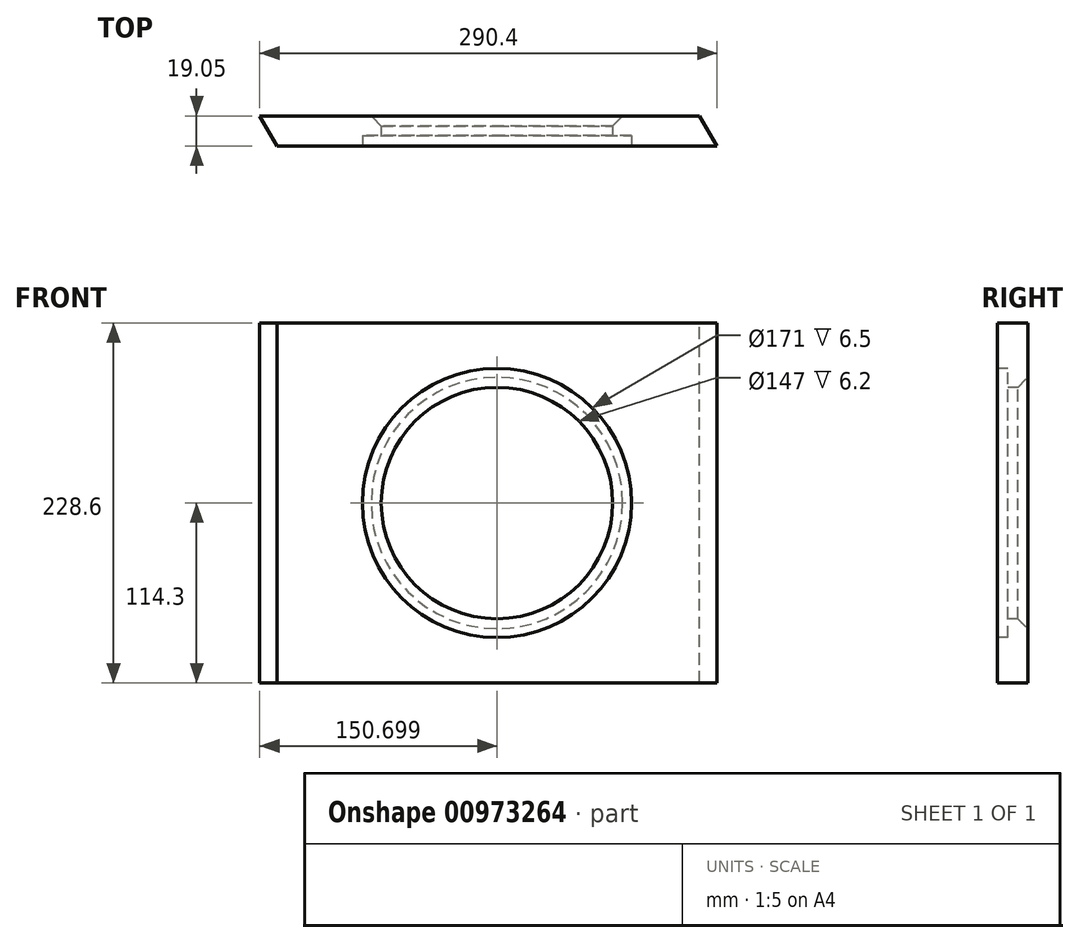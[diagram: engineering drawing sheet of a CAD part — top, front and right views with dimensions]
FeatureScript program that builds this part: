
annotation { "Feature Type Name" : "Feature", "Feature Type Description" : "" }
export const myFeature = defineFeature(function(context is Context, id is Id, definition is map)
    precondition{}
    {
        {
            var Q0;
            Q0=qCreatedBy(makeId("Front.planeOp"),FACE);
            var sketch = newSketch(context, id + "F0", { "sketchPlane" : qUnion([Q0])});
            skLineSegment(sketch, "E0.bottom", {"start": v(145.2, -114.3) * mm, "end": v(-145.2, -114.3) * mm});
            skLineSegment(sketch, "E0.top", {"start": v(145.2, 114.3) * mm, "end": v(-145.2, 114.3) * mm});
            skLineSegment(sketch, "E0.left", {"start": v(145.2, -114.3) * mm, "end": v(145.2, 114.3) * mm});
            skLineSegment(sketch, "E0.right", {"start": v(-145.2, -114.3) * mm, "end": v(-145.2, 114.3) * mm});
            skPoint(sketch, "E0.middle", {"position": v(0, 0) * mm});
            skSolve(sketch);
        }
        {
            var Q0;
            Q0=makeQuery(id+"F0.imprint","IMPRINT",FACE,{"disambiguationData":[TD([[makeQuery(id+"F0.imprint","IMPRINT",EDGE,{"derivedFrom":sQuery(id+"F0.wireOp",EDGE,"E0.bottom")}),-1.0]])]});
            extrude(context, id + "F1", {"entities" : qUnion([Q0]), "depth" : 19.05 * mm, "offsetDistance" : 25.4 * mm});
        }
        {
            var Q0;
            Q0=makeQuery(id+"F1.opExtrude","SWEPT_FACE",FACE,{"disambiguationData":[OSD([sQuery(id+"F0.wireOp",EDGE,"E0.top")])]});
            var sketch = newSketch(context, id + "F2", { "sketchPlane" : qUnion([Q0])});
            skLineSegment(sketch, "E1", {"start": v(-145.2, 0) * mm, "end": v(-134.2, -19.05) * mm});
            skLineSegment(sketch, "E2", {"start": v(-145.2, 0) * mm, "end": v(-145.2, -19.05) * mm});
            skLineSegment(sketch, "E3", {"start": v(-145.2, -19.05) * mm, "end": v(-134.2, -19.05) * mm});
            skLineSegment(sketch, "E4", {"start": v(145.2, -19.05) * mm, "end": v(134.2, 0) * mm});
            skLineSegment(sketch, "E5", {"start": v(134.2, 0) * mm, "end": v(145.2, 0) * mm});
            skLineSegment(sketch, "E6", {"start": v(145.2, 0) * mm, "end": v(145.2, -19.05) * mm});
            skSolve(sketch);
        }
        {
            var Q0;
            Q0 = qSketchRegion(id + "F2", true);
            extrude(context, id + "F3", {"entities" : qUnion([Q0]), "operationType" : NewBodyOperationType.REMOVE, "endBound" : BoundingType.THROUGH_ALL, "oppositeDirection" : true, "depth" : 25.4 * mm, "offsetDistance" : 25.4 * mm});
        }
        {
            var Q0;
            Q0=makeQuery(id+"F1.opExtrude","CAP_FACE",FACE,{"disambiguationData":[OSD([sQuery(id+"F0.wireOp",EDGE,"E0.bottom"),sQuery(id+"F0.wireOp",EDGE,"E0.top"),sQuery(id+"F0.wireOp",EDGE,"E0.left"),sQuery(id+"F0.wireOp",EDGE,"E0.right")])],"isStart":false});
            var sketch = newSketch(context, id + "F4", { "sketchPlane" : qUnion([Q0])});
            skLineSegment(sketch, "E7", {"start": v(5.5, 114.3) * mm, "end": v(5.5, -114.3) * mm, "construction": true});
            skLineSegment(sketch, "E8", {"start": v(-134.2, 0) * mm, "end": v(145.2, 0) * mm, "construction": true});
            skCircle(sketch, "E9", {"center": v(5.5, 0) * mm, "radius": 85.5 * mm});
            skSolve(sketch);
        }
        {
            var Q0;
            Q0 = qSketchRegion(id + "F4", true);
            extrude(context, id + "F5", {"entities" : qUnion([Q0]), "operationType" : NewBodyOperationType.REMOVE, "oppositeDirection" : true, "depth" : 6.5 * mm, "offsetDistance" : 25.4 * mm});
        }
        {
            var Q0;
            Q0=makeQuery(id+"F5.boolean.opBoolean","COPY",FACE,{"derivedFrom":makeQuery(id+"F5.opExtrude","CAP_FACE",FACE,{"disambiguationData":[OSD([sQuery(id+"F4.wireOp",EDGE,"E9")])],"isStart":false})});
            var sketch = newSketch(context, id + "F6", { "sketchPlane" : qUnion([Q0])});
            skLineSegment(sketch, "E10", {"start": v(-80, 0) * mm, "end": v(91, 0) * mm, "construction": true});
            skCircle(sketch, "E11", {"center": v(5.5, 0) * mm, "radius": 73.5 * mm});
            skSolve(sketch);
        }
        {
            var Q0;
            Q0 = qSketchRegion(id + "F6", true);
            extrude(context, id + "F7", {"entities" : qUnion([Q0]), "operationType" : NewBodyOperationType.REMOVE, "endBound" : BoundingType.THROUGH_ALL, "oppositeDirection" : true, "depth" : 25.4 * mm, "offsetDistance" : 25.4 * mm});
        }
        {
            var Q0;
            Q0=makeQuery(id+"F7.boolean.opBoolean","INTERSECT",EDGE,{"derivedFrom":[makeQuery(id+"F1.opExtrude","CAP_FACE",FACE,{"disambiguationData":[OSD([sQuery(id+"F0.wireOp",EDGE,"E0.bottom"),sQuery(id+"F0.wireOp",EDGE,"E0.top"),sQuery(id+"F0.wireOp",EDGE,"E0.left"),sQuery(id+"F0.wireOp",EDGE,"E0.right")])],"isStart":true}),makeQuery(id+"F7.opExtrude","SWEPT_FACE",FACE,{"disambiguationData":[OSD([sQuery(id+"F6.wireOp",EDGE,"E11")])]})]});
            chamfer(context, id + "F8", {"entities" : qUnion([Q0]), "width" : 6.35 * mm, "tangentPropagation" : true});
        }
    });
